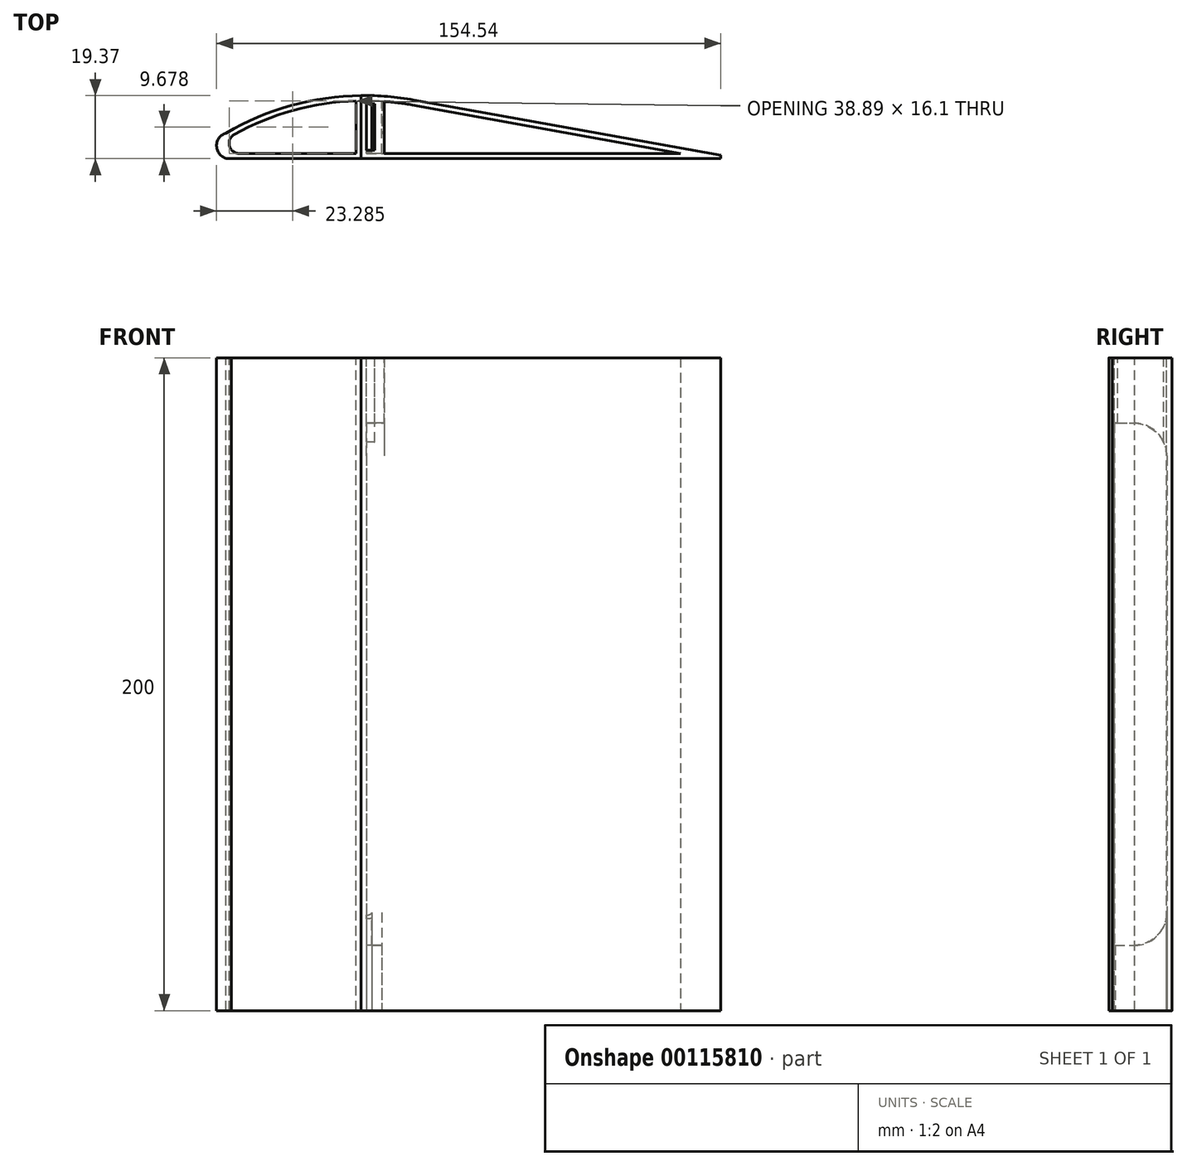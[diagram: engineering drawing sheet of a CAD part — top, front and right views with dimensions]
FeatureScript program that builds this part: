
annotation { "Feature Type Name" : "Feature", "Feature Type Description" : "" }
export const myFeature = defineFeature(function(context is Context, id is Id, definition is map)
    precondition{}
    {
        {
            var Q0;
            Q0=qCreatedBy(makeId("Top.planeOp"),FACE);
            var sketch = newSketch(context, id + "F0", { "sketchPlane" : qUnion([Q0])});
            skLineSegment(sketch, "E0", {"start": v(94.17, -2) * mm, "end": v(0, 15) * mm});
            skLineSegment(sketch, "E1", {"start": v(-55.86, -3) * mm, "end": v(94.14, -3) * mm});
            skLineSegment(sketch, "E2", {"start": v(94.14, -3) * mm, "end": v(94.17, -2) * mm});
            skArc(sketch, "E3", {"start": v(0, 15) * mm, "mid": v(-29.67, 15.05) * mm, "end": v(-57.5, 4.8) * mm});
            skArc(sketch, "E4", {"start": v(-57.5, 4.8) * mm, "mid": v(-60.28, 0.14) * mm, "end": v(-55.86, -3) * mm});
            skLineSegment(sketch, "E5", {"start": v(-16.04, 16.33) * mm, "end": v(-16.04, -3) * mm});
            skSolve(sketch);
        }
        {
            var Q0;
            {var subQ1=sQuery(id+"F0.wireOp",EDGE,"E0");Q0=makeQuery(id+"F0.imprint","IMPRINT",FACE,{"disambiguationData":[TD([[makeQuery(id+"F0.imprint","IMPRINT",EDGE,{"derivedFrom":subQ1}),1.0]])]});}
            extrude(context, id + "F1", {"entities" : qUnion([Q0]), "depth" : 200 * mm});
        }
        {
            var Q0;
            Q0=makeQuery(id+"F1.opExtrude","CAP_FACE",FACE,{"disambiguationData":[OSD([sQuery(id+"F0.wireOp",EDGE,"E0"),sQuery(id+"F0.wireOp",EDGE,"E1"),sQuery(id+"F0.wireOp",EDGE,"E2"),sQuery(id+"F0.wireOp",EDGE,"E3"),sQuery(id+"F0.wireOp",EDGE,"E4")])],"isStart":false});
            var sketch = newSketch(context, id + "F2", { "sketchPlane" : qUnion([Q0])});
            skLineSegment(sketch, "E6", {"start": v(94.17, -2) * mm, "end": v(0, 15) * mm});
            skLineSegment(sketch, "E7", {"start": v(-55.86, -3) * mm, "end": v(94.14, -3) * mm});
            skLineSegment(sketch, "E8", {"start": v(94.14, -3) * mm, "end": v(94.17, -2) * mm});
            skArc(sketch, "E9", {"start": v(0, 15) * mm, "mid": v(-29.67, 15.05) * mm, "end": v(-57.5, 4.8) * mm});
            skArc(sketch, "E10", {"start": v(-57.5, 4.8) * mm, "mid": v(-60.28, 0.14) * mm, "end": v(-55.86, -3) * mm});
            skLineSegment(sketch, "E11", {"start": v(-16.04, 16.33) * mm, "end": v(-16.04, -3) * mm});
            skSolve(sketch);
        }
        {
            var Q0;
            {var subQ2=sQuery(id+"F2.wireOp",EDGE,"E10");Q0=makeQuery(id+"F2.imprint","IMPRINT",FACE,{"disambiguationData":[TD([[makeQuery(id+"F2.imprint","IMPRINT",EDGE,{"derivedFrom":subQ2}),1.0]])]});}
            extrude(context, id + "F3", {"entities" : qUnion([Q0]), "oppositeDirection" : true, "depth" : 200 * mm});
        }
        {
            var Q0;
            Q0=makeQuery(id+"F1.opExtrude","CAP_FACE",FACE,{"disambiguationData":[OSD([sQuery(id+"F0.wireOp",EDGE,"E0"),sQuery(id+"F0.wireOp",EDGE,"E1"),sQuery(id+"F0.wireOp",EDGE,"E2"),sQuery(id+"F0.wireOp",EDGE,"E3"),sQuery(id+"F0.wireOp",EDGE,"E5")])],"isStart":false});
            var Q1;
            Q1=makeQuery(id+"F3.opExtrude","CAP_FACE",FACE,{"disambiguationData":[OSD([sQuery(id+"F2.wireOp",EDGE,"E7"),sQuery(id+"F2.wireOp",EDGE,"E9"),sQuery(id+"F2.wireOp",EDGE,"E10"),sQuery(id+"F2.wireOp",EDGE,"E11")])],"isStart":true});
            shell(context, id + "F4", {"entities" : qUnion([Q0, Q1]), "thickness" : 1.6 * mm});
        }
        {
            var Q0;
            Q0=makeQuery(id+"F4.opShell","OFFSET_FACE",FACE,{"disambiguationData":[OSD([sQuery(id+"F2.wireOp",EDGE,"E7"),sQuery(id+"F2.wireOp",EDGE,"E9"),sQuery(id+"F2.wireOp",EDGE,"E10"),sQuery(id+"F2.wireOp",EDGE,"E11")])]});
            var Q1;
            Q1=makeQuery(id+"F4.opShell","OFFSET_FACE",FACE,{"disambiguationData":[OSD([sQuery(id+"F0.wireOp",EDGE,"E0"),sQuery(id+"F0.wireOp",EDGE,"E1"),sQuery(id+"F0.wireOp",EDGE,"E2"),sQuery(id+"F0.wireOp",EDGE,"E3"),sQuery(id+"F0.wireOp",EDGE,"E5")])]});
            extrude(context, id + "F5", {"entities" : qUnion([Q0, Q1]), "operationType" : NewBodyOperationType.REMOVE, "endBound" : BoundingType.UP_TO_NEXT, "oppositeDirection" : true, "depth" : 25 * mm});
        }
        {
            var Q0;
            Q0=makeQuery(id+"F1.opExtrude","CAP_FACE",FACE,{"disambiguationData":[OSD([sQuery(id+"F0.wireOp",EDGE,"E0"),sQuery(id+"F0.wireOp",EDGE,"E1"),sQuery(id+"F0.wireOp",EDGE,"E2"),sQuery(id+"F0.wireOp",EDGE,"E3"),sQuery(id+"F0.wireOp",EDGE,"E5")])],"isStart":false});
            var sketch = newSketch(context, id + "F6", { "sketchPlane" : qUnion([Q0])});
            skLineSegment(sketch, "E12.bottom", {"start": v(-11.94, -1.4) * mm, "end": v(-8.94, -1.4) * mm});
            skLineSegment(sketch, "E12.top", {"start": v(-11.94, 14.74) * mm, "end": v(-8.94, 14.74) * mm});
            skLineSegment(sketch, "E12.left", {"start": v(-11.94, -1.4) * mm, "end": v(-11.94, 14.74) * mm});
            skLineSegment(sketch, "E12.right", {"start": v(-8.94, -1.4) * mm, "end": v(-8.94, 14.74) * mm});
            skLineSegment(sketch, "E13.bottom", {"start": v(-11.94, 14.74) * mm, "end": v(-14.44, 14.74) * mm});
            skLineSegment(sketch, "E13.top", {"start": v(-11.94, 13.74) * mm, "end": v(-14.44, 13.74) * mm});
            skLineSegment(sketch, "E13.left", {"start": v(-11.94, 14.74) * mm, "end": v(-11.94, 13.74) * mm});
            skLineSegment(sketch, "E13.right", {"start": v(-14.44, 14.74) * mm, "end": v(-14.44, 13.74) * mm});
            skLineSegment(sketch, "E14.bottom", {"start": v(-11.94, -1.4) * mm, "end": v(-14.44, -1.4) * mm});
            skLineSegment(sketch, "E14.top", {"start": v(-11.94, -0.4) * mm, "end": v(-14.44, -0.4) * mm});
            skLineSegment(sketch, "E14.left", {"start": v(-11.94, -1.4) * mm, "end": v(-11.94, -0.4) * mm});
            skLineSegment(sketch, "E14.right", {"start": v(-14.44, -1.4) * mm, "end": v(-14.44, -0.4) * mm});
            skSolve(sketch);
        }
        {
            var Q0;
            Q0 = qSketchRegion(id + "F6", true);
            extrude(context, id + "F7", {"entities" : qUnion([Q0]), "operationType" : NewBodyOperationType.ADD, "oppositeDirection" : true, "depth" : 20 * mm});
        }
        {
            var Q0;
            {var subQ0=sQuery(id+"F0.wireOp",EDGE,"E3");Q0=makeQuery(id+"F7.boolean.opBoolean","INTERSECT",EDGE,{"derivedFrom":[makeQuery(id+"F5.boolean.opBoolean","MERGE",FACE,{"derivedFrom":[makeQuery(id+"F4.opShell","OFFSET_FACE",FACE,{"disambiguationData":[OSD([subQ0])]})],"fromTools":[makeQuery(id+"F5.opExtrude","SWEPT_FACE",FACE,{"disambiguationData":[OSD([subQ0])]})]}),makeQuery(id+"F7.opExtrude","CAP_FACE",FACE,{"disambiguationData":[OSD([sQuery(id+"F6.wireOp",EDGE,"E12.bottom"),sQuery(id+"F6.wireOp",EDGE,"E12.top"),sQuery(id+"F6.wireOp",EDGE,"E12.left"),sQuery(id+"F6.wireOp",EDGE,"E12.right"),sQuery(id+"F6.wireOp",EDGE,"E13.bottom"),sQuery(id+"F6.wireOp",EDGE,"E13.top"),sQuery(id+"F6.wireOp",EDGE,"E13.right"),sQuery(id+"F6.wireOp",EDGE,"E14.bottom"),sQuery(id+"F6.wireOp",EDGE,"E14.top"),sQuery(id+"F6.wireOp",EDGE,"E14.right")])],"isStart":false})]});}
            var Q1;
            Q1=makeQuery(id+"F7.opExtrude","CAP_EDGE",EDGE,{"disambiguationData":[OSD([sQuery(id+"F6.wireOp",EDGE,"E12.bottom")])],"isStart":false});
            fillet(context, id + "F8", {"entities" : qUnion([Q0, Q1]), "radius" : 10 * mm, "tangentPropagation" : true, "allowEdgeOverflow" : false});
        }
        {
            var Q0;
            Q0=makeQuery(id+"F1.opExtrude","CAP_FACE",FACE,{"disambiguationData":[OSD([sQuery(id+"F0.wireOp",EDGE,"E0"),sQuery(id+"F0.wireOp",EDGE,"E1"),sQuery(id+"F0.wireOp",EDGE,"E2"),sQuery(id+"F0.wireOp",EDGE,"E3"),sQuery(id+"F0.wireOp",EDGE,"E5")])],"isStart":true});
            var sketch = newSketch(context, id + "F9", { "sketchPlane" : qUnion([Q0])});
            skLineSegment(sketch, "E15.bottom", {"start": v(-9.72, 1.4) * mm, "end": v(-12.77, 1.4) * mm});
            skLineSegment(sketch, "E15.top", {"start": v(-9.72, -14.71) * mm, "end": v(-12.77, -14.71) * mm});
            skLineSegment(sketch, "E15.left", {"start": v(-9.72, 1.4) * mm, "end": v(-9.72, -14.71) * mm});
            skLineSegment(sketch, "E15.right", {"start": v(-12.77, 1.4) * mm, "end": v(-12.77, -14.71) * mm});
            skLineSegment(sketch, "E16.bottom", {"start": v(-12.77, -14.71) * mm, "end": v(-14.44, -14.71) * mm});
            skLineSegment(sketch, "E16.top", {"start": v(-12.77, -14.56) * mm, "end": v(-14.44, -14.56) * mm});
            skLineSegment(sketch, "E16.left", {"start": v(-12.77, -14.71) * mm, "end": v(-12.77, -14.56) * mm});
            skLineSegment(sketch, "E16.right", {"start": v(-14.44, -14.71) * mm, "end": v(-14.44, -14.56) * mm});
            skLineSegment(sketch, "E17.bottom", {"start": v(-12.77, 1.4) * mm, "end": v(-14.44, 1.4) * mm});
            skLineSegment(sketch, "E17.top", {"start": v(-12.77, 1.17) * mm, "end": v(-14.44, 1.17) * mm});
            skLineSegment(sketch, "E17.left", {"start": v(-12.77, 1.4) * mm, "end": v(-12.77, 1.17) * mm});
            skLineSegment(sketch, "E17.right", {"start": v(-14.44, 1.4) * mm, "end": v(-14.44, 1.17) * mm});
            skSolve(sketch);
        }
        {
            var Q0;
            Q0 = qSketchRegion(id + "F9", true);
            extrude(context, id + "F10", {"entities" : qUnion([Q0]), "operationType" : NewBodyOperationType.ADD, "oppositeDirection" : true, "depth" : 20 * mm});
        }
        {
            var Q0;
            {var subQ0=sQuery(id+"F0.wireOp",EDGE,"E3");Q0=makeQuery(id+"F10.boolean.opBoolean","INTERSECT",EDGE,{"derivedFrom":[makeQuery(id+"F5.boolean.opBoolean","MERGE",FACE,{"derivedFrom":[makeQuery(id+"F4.opShell","OFFSET_FACE",FACE,{"disambiguationData":[OSD([subQ0])]})],"fromTools":[makeQuery(id+"F5.opExtrude","SWEPT_FACE",FACE,{"disambiguationData":[OSD([subQ0])]})]}),makeQuery(id+"F10.opExtrude","CAP_FACE",FACE,{"disambiguationData":[OSD([sQuery(id+"F9.wireOp",EDGE,"E15.bottom"),sQuery(id+"F9.wireOp",EDGE,"E15.top"),sQuery(id+"F9.wireOp",EDGE,"E15.left"),sQuery(id+"F9.wireOp",EDGE,"E15.right"),sQuery(id+"F9.wireOp",EDGE,"E16.bottom"),sQuery(id+"F9.wireOp",EDGE,"E16.top"),sQuery(id+"F9.wireOp",EDGE,"E16.right"),sQuery(id+"F9.wireOp",EDGE,"E17.bottom"),sQuery(id+"F9.wireOp",EDGE,"E17.top"),sQuery(id+"F9.wireOp",EDGE,"E17.right")])],"isStart":false})]});}
            var Q1;
            Q1=makeQuery(id+"F10.opExtrude","CAP_EDGE",EDGE,{"disambiguationData":[OSD([sQuery(id+"F9.wireOp",EDGE,"E15.bottom"),sQuery(id+"F9.wireOp",EDGE,"E17.bottom")])],"isStart":false});
            fillet(context, id + "F11", {"entities" : qUnion([Q0, Q1]), "radius" : 10 * mm, "tangentPropagation" : true, "allowEdgeOverflow" : false});
        }
        {
            var Q0;
            Q0=makeQuery(id+"F3.opExtrude","CAP_FACE",FACE,{"disambiguationData":[OSD([sQuery(id+"F2.wireOp",EDGE,"E7"),sQuery(id+"F2.wireOp",EDGE,"E9"),sQuery(id+"F2.wireOp",EDGE,"E10"),sQuery(id+"F2.wireOp",EDGE,"E11")])],"isStart":true});
            var sketch = newSketch(context, id + "F12", { "sketchPlane" : qUnion([Q0])});
            skArc(sketch, "E18", {"start": v(-56.89, 3.31) * mm, "mid": v(-61.64, -0.05) * mm, "end": v(-55.97, -1.4) * mm});
            skLineSegment(sketch, "E19", {"start": v(-56.89, 3.31) * mm, "end": v(-55.97, -1.4) * mm});
            skSolve(sketch);
        }
        {
            var Q0;
            Q0=makeQuery(id+"F12.imprint","IMPRINT",FACE,{"disambiguationData":[TD([[makeQuery(id+"F12.imprint","IMPRINT",EDGE,{"derivedFrom":sQuery(id+"F12.wireOp",EDGE,"E19")}),-1.0]])]});
            extrude(context, id + "F13", {"entities" : qUnion([Q0]), "operationType" : NewBodyOperationType.ADD, "oppositeDirection" : true, "depth" : 200 * mm});
        }
        {
            var Q0;
            {var subQ0=sQuery(id+"F2.wireOp",EDGE,"E10");var subQ1=sQuery(id+"F2.wireOp",EDGE,"E9");Q0=makeQuery(id+"F13.boolean.opBoolean","MERGE",EDGE,{"derivedFrom":[makeQuery(id+"F5.boolean.opBoolean","MERGE",EDGE,{"derivedFrom":[makeQuery(id+"F4.opShell","OFFSET_EDGE",EDGE,{"disambiguationData":[OSD([subQ1,subQ0])]})],"fromTools":[makeQuery(id+"F5.opExtrude","SWEPT_EDGE",EDGE,{"disambiguationData":[OSD([subQ1,subQ0])]})]}),makeQuery(id+"F13.opExtrude","SWEPT_EDGE",EDGE,{"disambiguationData":[OSD([subQ1,subQ0,sQuery(id+"F12.wireOp",EDGE,"E18"),sQuery(id+"F12.wireOp",EDGE,"E19")])]})]});}
            var Q1;
            {var subQ0=sQuery(id+"F2.wireOp",EDGE,"E10");var subQ1=sQuery(id+"F2.wireOp",EDGE,"E7");Q1=makeQuery(id+"F13.boolean.opBoolean","MERGE",EDGE,{"derivedFrom":[makeQuery(id+"F5.boolean.opBoolean","MERGE",EDGE,{"derivedFrom":[makeQuery(id+"F4.opShell","OFFSET_EDGE",EDGE,{"disambiguationData":[OSD([subQ1,subQ0])]})],"fromTools":[makeQuery(id+"F5.opExtrude","SWEPT_EDGE",EDGE,{"disambiguationData":[OSD([subQ1,subQ0])]})]}),makeQuery(id+"F13.opExtrude","SWEPT_EDGE",EDGE,{"disambiguationData":[OSD([subQ1,subQ0,sQuery(id+"F12.wireOp",EDGE,"E18"),sQuery(id+"F12.wireOp",EDGE,"E19")])]})]});}
            fillet(context, id + "F14", {"entities" : qUnion([Q0, Q1]), "radius" : 3 * mm, "tangentPropagation" : true, "allowEdgeOverflow" : false});
        }
    });
